# Revit family: Krome C9051-C9058 CP seris
name_source: partatom
category: Pipe Fittings
revit_build: Autodesk Revit 2018 (Build: 20170223_1515(x64)
units: mm (PartAtom-declared; Revit-internal decimal feet)

## family parameters
Always vertical = Yes
Cut with Voids When Loaded = No
Part Type = Elbow
Round Connector Dimension = Use Diameter
Shared = No
Work Plane-Based = No

## types (8) — shared parameters
Model = C9051-CP Series
URL = https://kromedispense.co.in

## per-type parameters (varying)
| type | Weight (Kgs) |
| C9051-CP-12" Fusion Grab Bar-Chrome Polished | .79 |
| C9052-CP-16" Fusion Grab Bar-Chrome Polished | .88 |
| C9053-CP-18" Fusion Grab Bar-Chrome Polished | .93 |
| C9054-CP-24" Fusion Grab Bar-Chrome Polished | 1.07 |
| C9055-CP-30" Fusion Grab Bar-Chrome Polished | 1.21 |
| C9056-CP-36" Fusion Grab Bar-Chrome Polished | 1..35 |
| C9057-CP-42" Fusion Grab Bar-Chrome Polished | 1.5 |
| C9058-CP-48" Fusion Grab Bar-Chrome Polished | 1.64 |

## geometry (parser evidence)
native form markers: Sweep x3
no freeform markers — native parametric forms only
